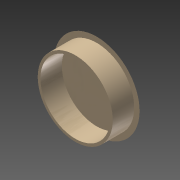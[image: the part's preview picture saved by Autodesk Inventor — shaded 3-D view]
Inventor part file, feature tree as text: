
AUTODESK INVENTOR PART (.ipt)
format: ipt  version: 2015 (Build 190159000, 159)  size: 113,664 bytes
history: native  units: mm
features: sketch x2, other x1, extrude x1, shell x1, revolve x1
ambient origin geometry x8: Origin, YZ Plane, XZ Plane, XY Plane, X Axis, Y Axis, Z Axis, Center Point
bodies: Body1 (feature_tree)
feature tree (6):
  other  "Bryła1"
  extrude  "Wyciągnięcie proste1"  Depth=28.0mm
  shell  "Skorupa1"  Thickness=8.0mm
  revolve  "Obrót1"
  sketch  "Szkic1"
  sketch  "Szkic2"
